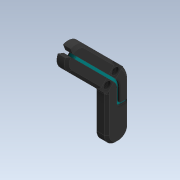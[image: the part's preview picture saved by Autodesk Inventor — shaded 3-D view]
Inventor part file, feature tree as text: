
AUTODESK INVENTOR PART (.ipt)
format: ipt  version: 2020 (Build 240168000, 168)  size: 501,248 bytes
history: native  units: in
note: dims shown in document units (in); Inventor stores cm internally (conversion verified against a paired STEP export)
features: sketch x30, other x8, projected_geometry x6, extrude x5, plane x4, chamfer x3
ambient origin geometry x8: Origin, YZ Plane, XZ Plane, XY Plane, X Axis, Y Axis, Z Axis, Center Point
bodies: Solid2 (feature_tree), Solid3 (feature_tree), Solid1 (feature_tree), Solid4 (feature_tree), Solid5 (feature_tree)
feature tree (56):
  other  "LegMidTop.ipt"
  extrude  "Extrusion3"  Depth=0.3937in
  extrude  "Extrusion4"  TaperAngle=90.0deg  [1 undecoded]
  extrude  "Extrusion5"  Depth=0.0787in
  chamfer  "Chamfer1"  Distance=0.3937in
  extrude  "Extrusion7"  Depth=0.0787in
  chamfer  "Chamfer2"  Distance=0.0984in
  chamfer  "Chamfer3"  Distance=0.0984in
  extrude  "Extrusion8"  Depth=0.0787in TaperAngle=0.0deg
  other  "Solid1::LegMidTop.ipt"
  other  "Solid2::LegMidTop.ipt"
  other  "Solid3::LegMidTop.ipt"
  other  "Solid4::LegMidTop.ipt"
  other  "Solid5::LegMidTop.ipt"
  other  "Solid6::LegMidTop.ipt"
  other  "TaggingFeature1"
  sketch  "Sketch1"  dims[d0=0.3937in d5=0.2362in]
  sketch  "Sketch2"  dims[d6=0.0394in d7=90.0deg]
  sketch  "Sketch3"  dims[d8=0.0787in d9=0.0197in]
  sketch  "Sketch4"  dims[d10=0.0394in]
  sketch  "Sketch5"  dims[d11=0.0591in d12=0.3937in d13=0.0in]
  sketch  "Sketch12"  dims[d14=0.0787in d15=0.315in]
  sketch  "Sketch14"  dims[d16=0.3937in]
  sketch  "Sketch15"  dims[d17=0.0787in]
  sketch  "Sketch16"  dims[d20=0.0in]
  sketch  "Sketch17"  dims[d21=0.315in]
  sketch  "Sketch19"  dims[d22=0.2756in]
  sketch  "Sketch22"  dims[d23=0.0787in]
  sketch  "Sketch23"  dims[d24=0.0354in]
  sketch  "Sketch24"  dims[d25=0.1142in d26=0.0984in d27=0.0in]
  sketch  "Sketch25"  dims[d28=0.0787in d29=0.0984in d30=0.0in]
  sketch  "Sketch26"  dims[d35=0.0787in d36=0.0787in d37=45.0deg d38=0.6688in d39=0.0in]
  sketch  "Sketch27"  dims[d40=0.0787in d41=0.0787in d42=45.0deg]
  sketch  "Sketch28"  dims[d43=0.0787in d44=0.0787in d45=45.0deg]
  sketch  "Sketch29"  dims[d46=0.0039in]
  sketch  "Sketch30"  dims[d47=0.3937in d48=0.0in]
  sketch  "Sketch31"  dims[d3=0.0197in]
  sketch  "Sketch32"  dims[d4=0.0344in]
  sketch  "Sketch33"
  sketch  "Sketch39"
  sketch  "Sketch40"
  plane  "Work Plane1"
  plane  "Work Plane2"
  plane  "Work Plane3"
  plane  "Work Plane4"
  sketch  "Sketch44"
  projected_geometry  "Projected Loop5"
  sketch  "Sketch45"
  projected_geometry  "Projected Loop6"
  projected_geometry  "Projected Loop7"
  sketch  "Sketch46"
  projected_geometry  "Projected Loop8"
  sketch  "Sketch48"
  projected_geometry  "Projected Loop11"
  sketch  "Sketch49"
  projected_geometry  "Projected Loop12"
note: 1 required parameter value undecoded (feature->parameter linkage not recoverable at this tier; creation-order binding heuristic only, values carry confidence <= 0.55)
